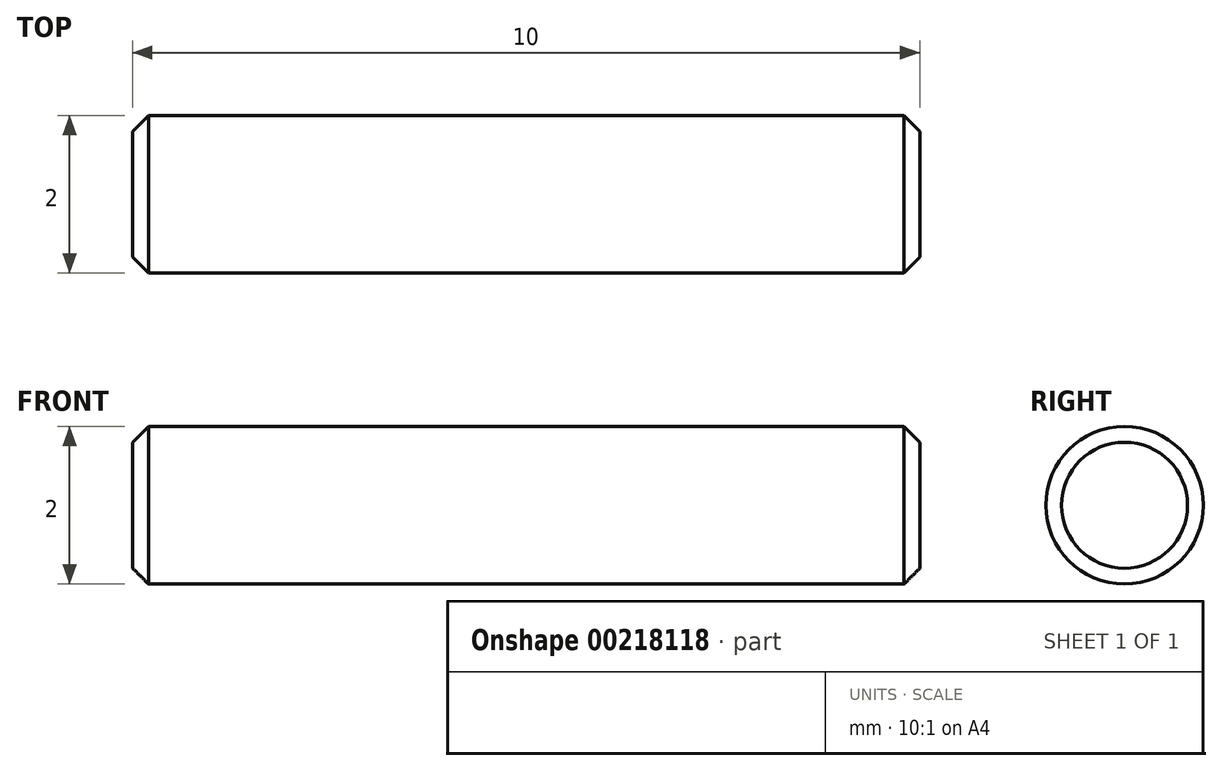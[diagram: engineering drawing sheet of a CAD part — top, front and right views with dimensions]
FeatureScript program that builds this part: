
annotation { "Feature Type Name" : "Feature", "Feature Type Description" : "" }
export const myFeature = defineFeature(function(context is Context, id is Id, definition is map)
    precondition{}
    {
        {
            var Q0;
            Q0=qCreatedBy(makeId("Right.planeOp"),FACE);
            var sketch = newSketch(context, id + "F0", { "sketchPlane" : qUnion([Q0])});
            skCircle(sketch, "E0", {"center": v(0, 0) * mm, "radius": 1 * mm});
            skSolve(sketch);
        }
        {
            var Q0;
            Q0=makeQuery(id+"F0.imprint","IMPRINT",FACE,{"disambiguationData":[TD([[makeQuery(id+"F0.imprint","IMPRINT",EDGE,{"derivedFrom":sQuery(id+"F0.wireOp",EDGE,"E0")}),1.0]])]});
            extrude(context, id + "F1", {"entities" : qUnion([Q0]), "depth" : 10 * mm});
        }
        {
            var Q0;
            Q0=makeQuery(id+"F1.opExtrude","CAP_EDGE",EDGE,{"disambiguationData":[OSD([sQuery(id+"F0.wireOp",EDGE,"E0")])],"isStart":false});
            var Q1;
            Q1=makeQuery(id+"F1.opExtrude","CAP_EDGE",EDGE,{"disambiguationData":[OSD([sQuery(id+"F0.wireOp",EDGE,"E0")])],"isStart":true});
            chamfer(context, id + "F2", {"entities" : qUnion([Q0, Q1]), "width" : .2 * mm, "tangentPropagation" : true});
        }
    });
